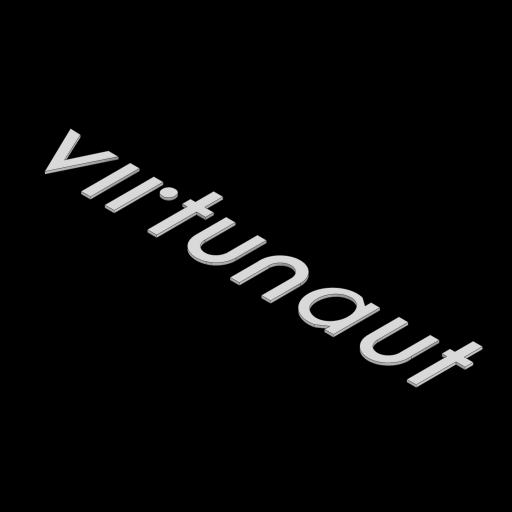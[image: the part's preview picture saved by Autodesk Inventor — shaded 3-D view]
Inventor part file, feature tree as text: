
AUTODESK INVENTOR PART (.ipt)
format: ipt  version: 2024 (Build 280153000, 153)  size: 476,160 bytes
history: native  units: mm
features: projected_geometry x10, extrude x3, sketch x3
ambient origin geometry x8: Origin, YZ Plane, XZ Plane, XY Plane, X Axis, Y Axis, Z Axis, Center Point
bodies: Volumenkörper1 (feature_tree)
feature tree (16):
  extrude  "Extrusion1"  Depth=0.6mm
  extrude  "Extrusion2"  Depth=0.25mm
  extrude  "Extrusion3"  Depth=0.12mm
  sketch  "Skizze1"  dims[d0=0.6mm d1=0.0mm d2=0.25mm]
  sketch  "Skizze3"  dims[d3=0.25mm d4=0.25mm]
  projected_geometry  "Projizierte Kontur11"
  projected_geometry  "Projizierte Kontur12"
  projected_geometry  "Projizierte Kontur13"
  projected_geometry  "Projizierte Kontur14"
  projected_geometry  "Projizierte Kontur15"
  projected_geometry  "Projizierte Kontur16"
  projected_geometry  "Projizierte Kontur17"
  projected_geometry  "Projizierte Kontur18"
  projected_geometry  "Projizierte Kontur19"
  projected_geometry  "Projizierte Kontur20"
  sketch  "Skizze4"  dims[d5=0.25mm d6=0.12mm d7=0.25mm d8=0.25mm d9=0.25mm d10=0.25mm d11=0.25mm d14=0.7mm d15=0.0mm d16=0.7mm d17=0.0mm]
